# Revit family: Fire-Smoke-Curtain_Elevator-Prot_DoorSystems_DSI-600
name_source: partatom
category: Generic Models
revit_build: Autodesk Revit 2018 (Build: 20190510_1515(x64)
units: mm (PartAtom-declared; Revit-internal decimal feet)

## family parameters
Always vertical = No
Can host rebar = No
Cut with Voids When Loaded = No
OmniClass Number = 23.30.10.21
OmniClass Title = Special Function Doors
Part Type = Normal
Room Calculation Point = No
Round Connector Dimension = Use Diameter
Shared = No
Work Plane-Based = Yes

## types (1)
- Single Roller
    Assembly Code = D4090
    Construction Details = http://www.arcat.com
    Default Elevation = 0' - 0"
    Description = Door Systems Inc Fire Rated Elevator Smoke Curtain - DSI-600 as Specified
    Electrical_Voltage = 24 V
    Expected Lifespan (Years) = 0
    Fire Performance = UL 10D 1 HR  ;  California Fire State Marshall
    Keynote = 08 34 84
    Maintenance Schedule (Months) = 0
    Manufacturer = Door Systems, Inc
    Manufacturer Website = http://www.doorsysinc.com
    Maximum Size = 19 ft Wide. Heights Above 11 ft Require Larger Head Clearances
    Model = DSI 600-60GS
    Product Data = http://www.arcat.com
    Product Properties = http://www.doorsysinc.com
    Revision = R1_2016-07
    Sales Information = http://www.doorsysinc.com
    Specification = http://www.arcat.com
    Standards Conformance = ICC  ;  UL 1784 S Label  ;  UL 864  ;  OSHPD  ;  LAFD High Rise
    URL = http://www.doorsysinc.com
    Warranty Duration (Years) = 0
    mrou = No
    mrsbs = No

## geometry (parser evidence)
native form markers: Sweep x3
no freeform markers — native parametric forms only
